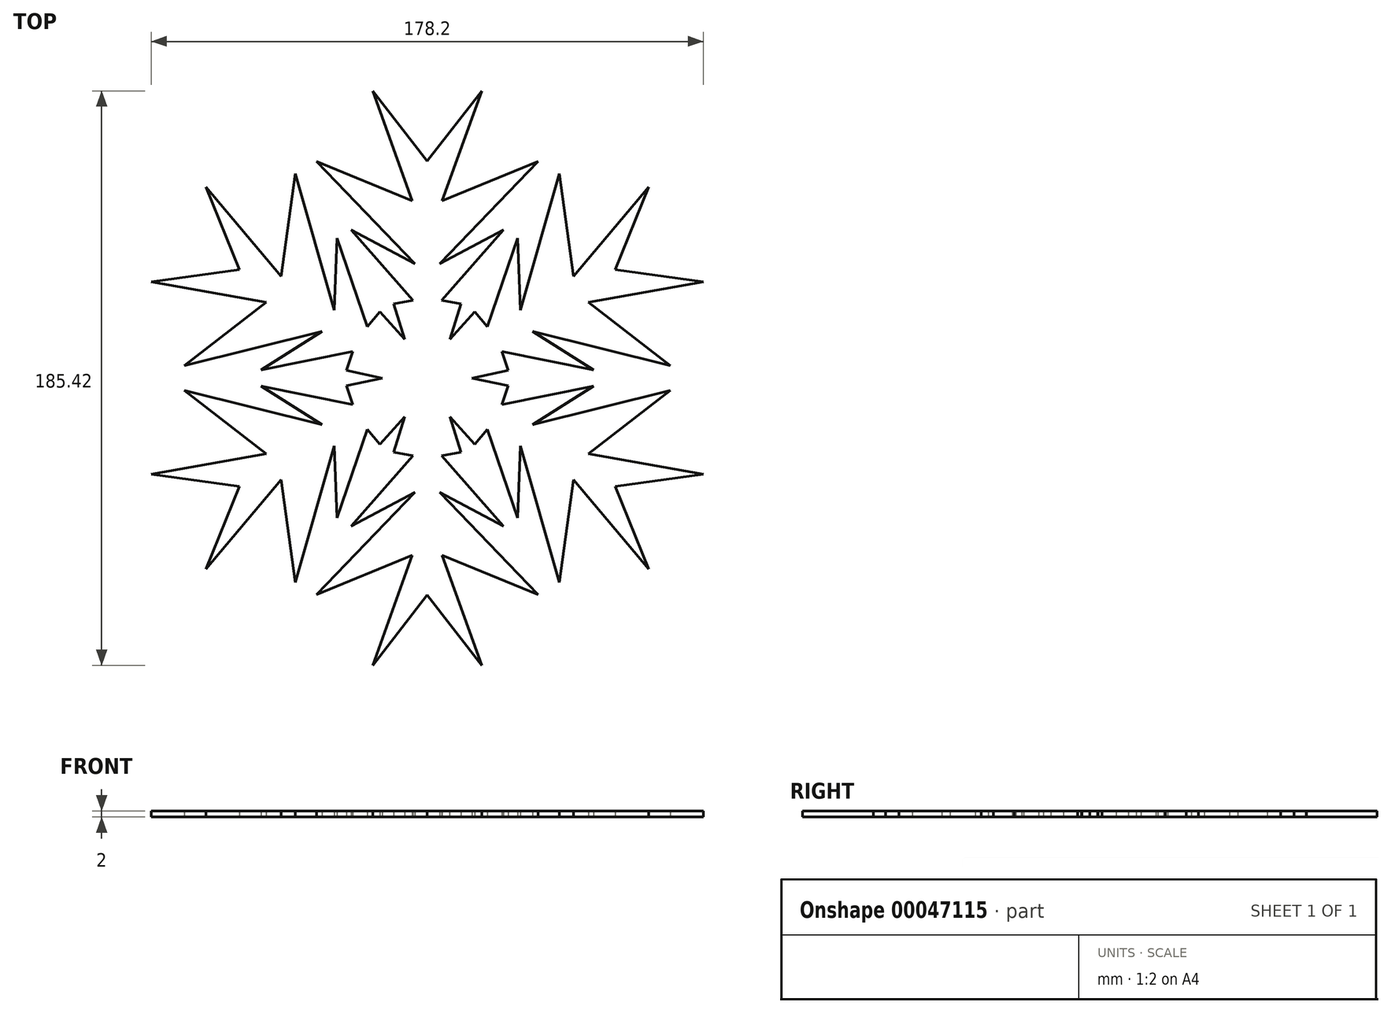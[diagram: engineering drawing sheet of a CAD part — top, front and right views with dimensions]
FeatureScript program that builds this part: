
annotation { "Feature Type Name" : "Feature", "Feature Type Description" : "" }
export const myFeature = defineFeature(function(context is Context, id is Id, definition is map)
    precondition{}
    {
        {
            var Q0;
            Q0=qCreatedBy(makeId("Top.planeOp"),FACE);
            var sketch = newSketch(context, id + "F0", { "sketchPlane" : qUnion([Q0])});
            skLineSegment(sketch, "E0", {"start": v(0, 0) * mm, "end": v(0, 95) * mm, "construction": true});
            skLineSegment(sketch, "E1", {"start": v(24.53, 47.78) * mm, "end": v(4, 36.93) * mm});
            skLineSegment(sketch, "E2", {"start": v(4, 36.93) * mm, "end": v(35.76, 69.9) * mm});
            skLineSegment(sketch, "E3", {"start": v(35.76, 69.9) * mm, "end": v(4.83, 57.23) * mm});
            skLineSegment(sketch, "E4", {"start": v(4.83, 57.23) * mm, "end": v(17.62, 92.71) * mm});
            skLineSegment(sketch, "E5", {"start": v(17.62, 92.71) * mm, "end": v(0, 70.04) * mm});
            skLineSegment(sketch, "E6", {"start": v(3.22, 0) * mm, "end": v(0, 0) * mm});
            skLineSegment(sketch, "E7", {"start": v(0, 0) * mm, "end": v(0, 70.04) * mm});
            skLineSegment(sketch, "E8", {"start": v(24.53, 47.78) * mm, "end": v(4.63, 25.08) * mm});
            skLineSegment(sketch, "E9", {"start": v(4.63, 25.08) * mm, "end": v(10.88, 23.89) * mm});
            skLineSegment(sketch, "E10", {"start": v(10.88, 23.89) * mm, "end": v(3.22, 0) * mm});
            skSolve(sketch);
        }
        {
            var Q0;
            Q0=makeQuery(id+"F0.imprint","IMPRINT",FACE,{"disambiguationData":[TD([[makeQuery(id+"F0.imprint","IMPRINT",EDGE,{"derivedFrom":sQuery(id+"F0.wireOp",EDGE,"E1")}),1.0]])]});
            extrude(context, id + "F1", {"entities" : qUnion([Q0]), "depth" : 2 * mm});
        }
        {
            var Q0;
            Q0=makeQuery(id+"F1.opExtrude","SWEPT_BODY",BODY,{"disambiguationData":[OSD([sQuery(id+"F0.wireOp",EDGE,"48c96cab-7b97-40db-923f-d73ac41cfb98"),sQuery(id+"F0.wireOp",EDGE,"E1"),sQuery(id+"F0.wireOp",EDGE,"E2"),sQuery(id+"F0.wireOp",EDGE,"E3"),sQuery(id+"F0.wireOp",EDGE,"E4"),sQuery(id+"F0.wireOp",EDGE,"E5"),sQuery(id+"F0.wireOp",EDGE,"67989d3d-554a-4a09-a72c-a1e81bb6601a"),sQuery(id+"F0.wireOp",EDGE,"E6")])]});
            var Q1;
            Q1=qCreatedBy(makeId("Right.planeOp"),FACE);
            mirror(context, id + "F2", {"operationType" : NewBodyOperationType.ADD, "entities" : qUnion([Q0]), "mirrorPlane" : qUnion([Q1])});
        }
        {
            var Q0;
            Q0=qCreatedBy(makeId("Front.planeOp"),FACE);
            var sketch = newSketch(context, id + "F3", { "sketchPlane" : qUnion([Q0])});
            skLineSegment(sketch, "E11", {"start": v(0, 0) * mm, "end": v(0, 8.23) * mm});
            skSolve(sketch);
        }
        {
            var Q0;
            Q0=makeQuery(id+"F1.opExtrude","SWEPT_BODY",BODY,{"disambiguationData":[OSD([sQuery(id+"F0.wireOp",EDGE,"48c96cab-7b97-40db-923f-d73ac41cfb98"),sQuery(id+"F0.wireOp",EDGE,"E1"),sQuery(id+"F0.wireOp",EDGE,"E2"),sQuery(id+"F0.wireOp",EDGE,"E3"),sQuery(id+"F0.wireOp",EDGE,"E4"),sQuery(id+"F0.wireOp",EDGE,"E5"),sQuery(id+"F0.wireOp",EDGE,"67989d3d-554a-4a09-a72c-a1e81bb6601a"),sQuery(id+"F0.wireOp",EDGE,"E6")])]});
            var Q1;
            Q1=sQuery(id+"F3.wireOp",EDGE,"E11");
            circularPattern(context, id + "F4", {"operationType" : NewBodyOperationType.ADD, "entities" : qUnion([Q0]), "axis" : qUnion([Q1]), "angle" : 60 * degree, "instanceCount" : 6});
        }
    });
